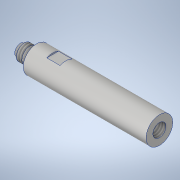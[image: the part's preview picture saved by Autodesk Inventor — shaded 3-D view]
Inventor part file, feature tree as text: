
AUTODESK INVENTOR PART (.ipt)
format: ipt  version: 2020 (Build 240168000, 168)  size: 167,936 bytes
history: native  units: mm
features: thread x3, sketch x3, extrude x2, chamfer x2, revolve x1, hole x1, fillet x1, projected_geometry x1
ambient origin geometry x8: Origin, YZ Plane, XZ Plane, XY Plane, X Axis, Y Axis, Z Axis, Center Point
bodies: Volumenkörper1 (feature_tree)
feature tree (14):
  revolve  "Umdrehung1"
  hole  "Bohrung1"  [1 undecoded]
  extrude  "Extrusion1"  TaperAngle=90.0deg  [1 undecoded]
  chamfer  "Chamfer6"  Distance=10.0mm
  chamfer  "Chamfer7"  Distance=46.0mm
  fillet  "Fillet3"  Radius=4.4mm
  thread  "Thread3"  [1 undecoded]
  extrude  "Extrusion2"  Depth=35.0mm TaperAngle=0.0deg
  thread  "Thread2"  [1 undecoded]
  thread  "Gewinde1"  [1 undecoded]
  sketch  "Skizze1"  dims[d1=6.0mm d2=10.0mm]
  sketch  "Skizze2"  dims[d3=6.0mm d4=90.0deg]
  sketch  "Sketch4"  dims[d5=4.917mm d6=9.0mm d7=4.0mm d8=2.0mm d9=90.0deg d10=13.0mm d11=20.594885mm d12=10.0mm d13=0.0mm d17=46.0mm d21=4.4mm d22=1.1mm d23=0.0mm d28=5.286mm d29=0.0mm d37=1.4mm d38=0.8mm d39=30.0deg d40=1.4mm d41=0.8mm d42=30.0deg d43=0.6mm d44=4.1mm d45=0.0mm d46=5.0mm d47=0.5mm d48=5.0mm d49=0.5mm d50=35.0mm d51=35.0mm d52=1.561mm d53=0.0mm]
  projected_geometry  "Projected Loop1"
note: 5 required parameter values undecoded (feature->parameter linkage not recoverable at this tier; creation-order binding heuristic only, values carry confidence <= 0.55)
